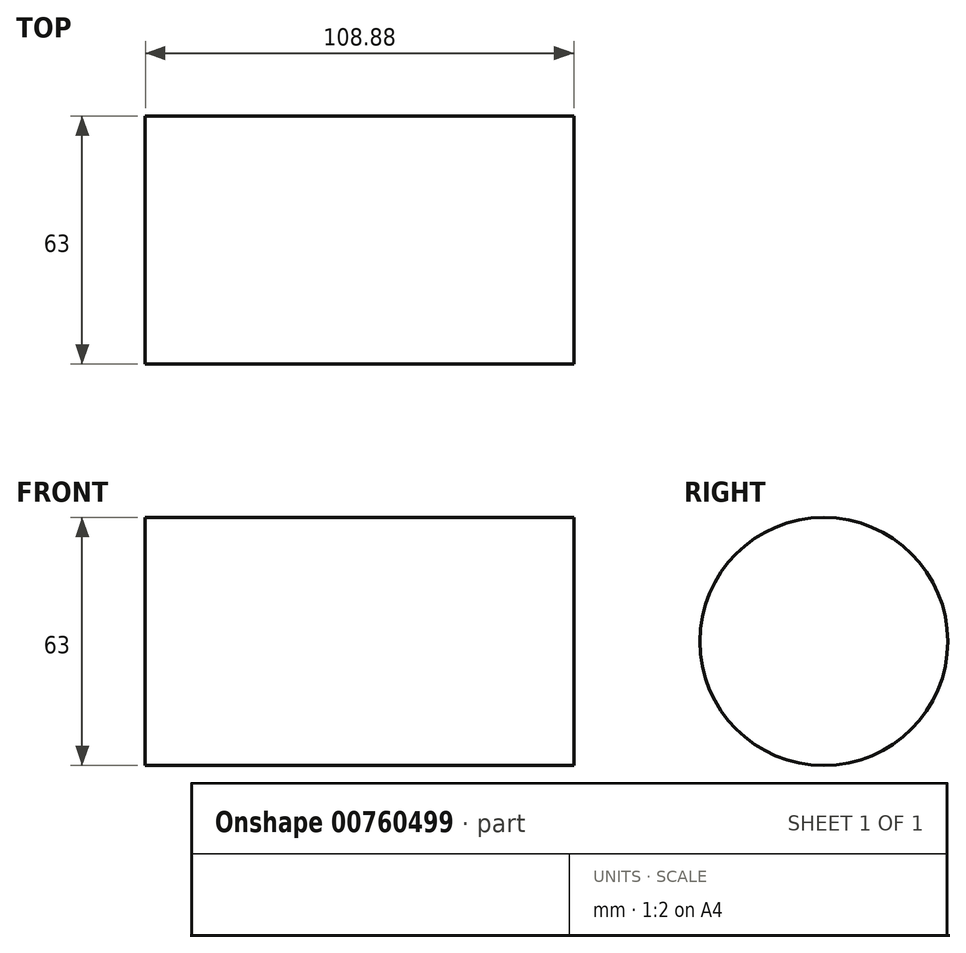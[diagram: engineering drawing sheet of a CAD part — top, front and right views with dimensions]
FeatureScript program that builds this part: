
annotation { "Feature Type Name" : "Feature", "Feature Type Description" : "" }
export const myFeature = defineFeature(function(context is Context, id is Id, definition is map)
    precondition{}
    {
        {
            var Q0;
            Q0=qCreatedBy(makeId("Front.planeOp"),FACE);
            var sketch = newSketch(context, id + "F0", { "sketchPlane" : qUnion([Q0])});
            skLineSegment(sketch, "E0.bottom", {"start": v(54.44, 31.5) * mm, "end": v(-54.44, 31.5) * mm});
            skLineSegment(sketch, "E0.left", {"start": v(54.44, 31.5) * mm, "end": v(54.44, 0) * mm});
            skLineSegment(sketch, "E0.right", {"start": v(-54.44, 31.5) * mm, "end": v(-54.44, 0) * mm});
            skPoint(sketch, "E0.middle", {"position": v(0, 0) * mm});
            skLineSegment(sketch, "E1", {"start": v(-54.44, 0) * mm, "end": v(54.44, 0) * mm});
            skPoint(sketch, "E0.top.end.orphan", {"position": v(-54.44, -31.5) * mm});
            skPoint(sketch, "E2.end.orphan", {"position": v(54.44, -31.5) * mm});
            skSolve(sketch);
        }
        {
            var Q0;
            Q0=makeQuery(id+"F0.imprint","IMPRINT",FACE,{"disambiguationData":[TD([[makeQuery(id+"F0.imprint","IMPRINT",EDGE,{"derivedFrom":sQuery(id+"F0.wireOp",EDGE,"E0.bottom")}),1.0]])]});
            var Q1;
            Q1=sQuery(id+"F0.wireOp",EDGE,"E1");
            revolve(context, id + "F1", {"surfaceOperationType" : NewSurfaceOperationType.NEW, "entities" : qUnion([Q0]), "axis" : qUnion([Q1]), "revolveType" : RevolveType.FULL});
        }
    });
